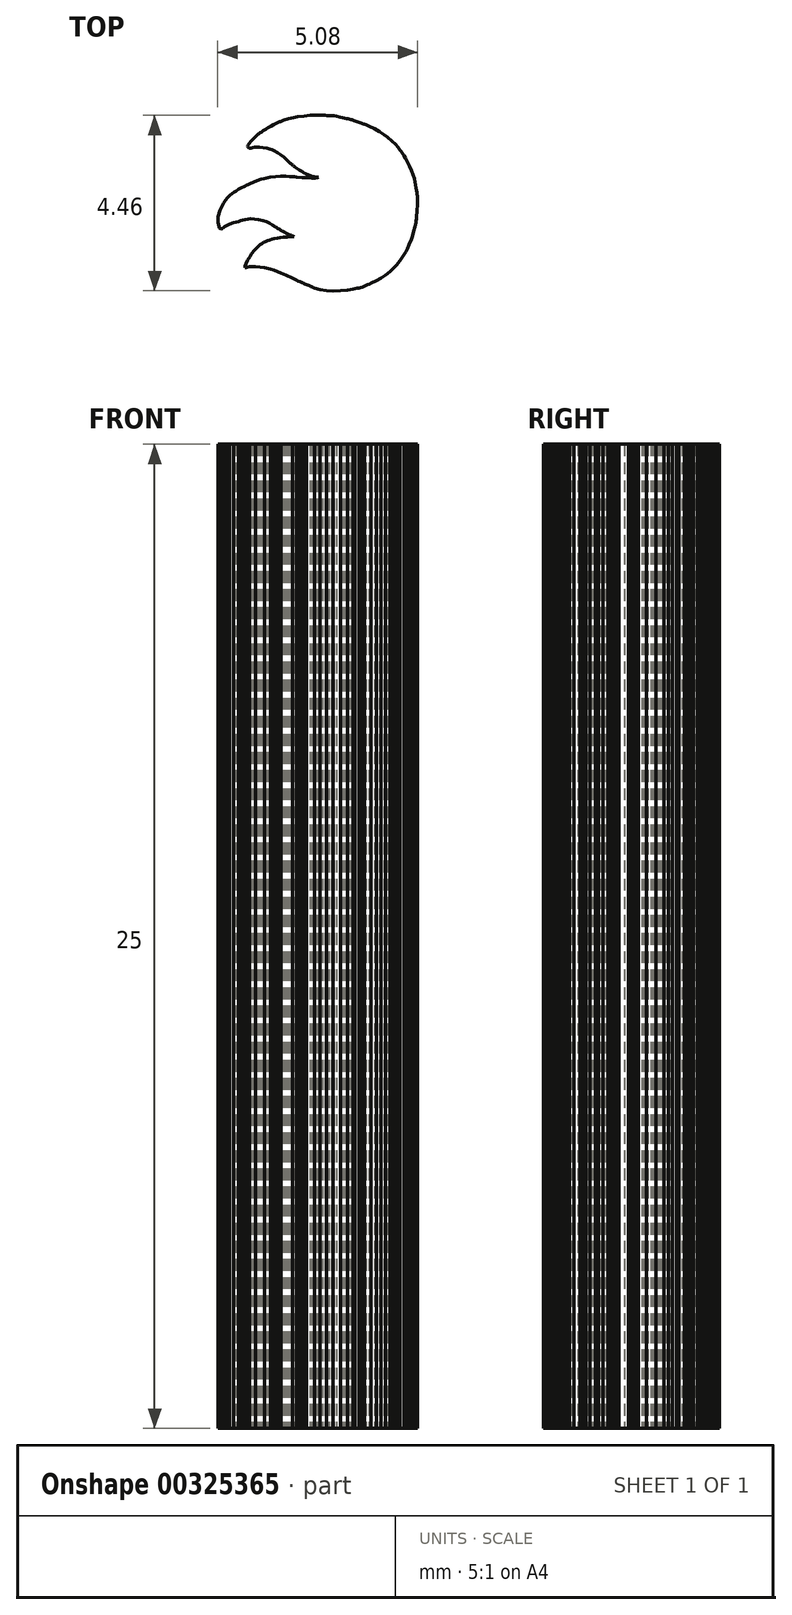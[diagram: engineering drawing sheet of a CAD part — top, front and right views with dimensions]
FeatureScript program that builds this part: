
annotation { "Feature Type Name" : "Feature", "Feature Type Description" : "" }
export const myFeature = defineFeature(function(context is Context, id is Id, definition is map)
    precondition{}
    {
        {
            var Q0;
            Q0=qCreatedBy(makeId("Top.planeOp"),FACE);
            var sketch = newSketch(context, id + "F0", { "sketchPlane" : qUnion([Q0])});
            skLineSegment(sketch, "E0.bottom", {"start": v(-35.48, 36.06) * mm, "end": v(-0.48, 36.06) * mm});
            skLineSegment(sketch, "E0.top", {"start": v(-35.48, 6.06) * mm, "end": v(-0.48, 6.06) * mm});
            skLineSegment(sketch, "E0.left", {"start": v(-35.48, 36.06) * mm, "end": v(-35.48, 6.06) * mm});
            skLineSegment(sketch, "E0.right", {"start": v(-0.48, 36.06) * mm, "end": v(-0.48, 6.06) * mm});
            skPoint(sketch, "E1", {"position": v(-0.48, 21.06) * mm});
            skArc(sketch, "E2", {"start": v(-0.48, 6.06) * mm, "mid": v(14.52, 21.06) * mm, "end": v(-0.48, 36.06) * mm});
            skLineSegment(sketch, "E3", {"start": v(0.23, -2.23) * mm, "end": v(0.06, -2.2) * mm});
            skLineSegment(sketch, "E4", {"start": v(0.06, -2.2) * mm, "end": v(-0.08, -2.16) * mm});
            skLineSegment(sketch, "E5", {"start": v(-0.08, -2.16) * mm, "end": v(-0.1, -2.16) * mm});
            skLineSegment(sketch, "E6", {"start": v(-0.1, -2.16) * mm, "end": v(-0.1, -2.15) * mm});
            skLineSegment(sketch, "E7", {"start": v(-0.1, -2.15) * mm, "end": v(-0.12, -2.14) * mm});
            skLineSegment(sketch, "E8", {"start": v(-0.12, -2.14) * mm, "end": v(-0.13, -2.14) * mm});
            skLineSegment(sketch, "E9", {"start": v(-0.13, -2.14) * mm, "end": v(-0.15, -2.13) * mm});
            skLineSegment(sketch, "E10", {"start": v(-0.15, -2.13) * mm, "end": v(-0.18, -2.12) * mm});
            skLineSegment(sketch, "E11", {"start": v(-0.18, -2.12) * mm, "end": v(-0.2, -2.1) * mm});
            skLineSegment(sketch, "E12", {"start": v(-0.2, -2.1) * mm, "end": v(-0.25, -2.09) * mm});
            skLineSegment(sketch, "E13", {"start": v(-0.25, -2.09) * mm, "end": v(-0.29, -2.07) * mm});
            skLineSegment(sketch, "E14", {"start": v(-0.29, -2.07) * mm, "end": v(-0.32, -2.06) * mm});
            skLineSegment(sketch, "E15", {"start": v(-0.32, -2.06) * mm, "end": v(-0.34, -2.04) * mm});
            skLineSegment(sketch, "E16", {"start": v(-0.34, -2.04) * mm, "end": v(-0.36, -2.04) * mm});
            skLineSegment(sketch, "E17", {"start": v(-0.36, -2.04) * mm, "end": v(-0.38, -2.03) * mm});
            skLineSegment(sketch, "E18", {"start": v(-0.38, -2.03) * mm, "end": v(-0.4, -2.02) * mm});
            skLineSegment(sketch, "E19", {"start": v(-0.4, -2.02) * mm, "end": v(-0.45, -2) * mm});
            skLineSegment(sketch, "E20", {"start": v(-0.45, -2) * mm, "end": v(-0.5, -1.98) * mm});
            skLineSegment(sketch, "E21", {"start": v(-0.5, -1.98) * mm, "end": v(-0.54, -1.96) * mm});
            skLineSegment(sketch, "E22", {"start": v(-0.54, -1.96) * mm, "end": v(-0.64, -1.91) * mm});
            skLineSegment(sketch, "E23", {"start": v(-0.64, -1.91) * mm, "end": v(-0.81, -1.83) * mm});
            skLineSegment(sketch, "E24", {"start": v(-0.81, -1.83) * mm, "end": v(-0.93, -1.78) * mm});
            skLineSegment(sketch, "E25", {"start": v(-0.93, -1.78) * mm, "end": v(-1.03, -1.74) * mm});
            skLineSegment(sketch, "E26", {"start": v(-1.03, -1.74) * mm, "end": v(-1.1, -1.7) * mm});
            skLineSegment(sketch, "E27", {"start": v(-1.1, -1.7) * mm, "end": v(-1.2, -1.68) * mm});
            skLineSegment(sketch, "E28", {"start": v(-1.2, -1.68) * mm, "end": v(-1.35, -1.65) * mm});
            skLineSegment(sketch, "E29", {"start": v(-1.35, -1.65) * mm, "end": v(-1.58, -1.62) * mm});
            skLineSegment(sketch, "E30", {"start": v(-1.58, -1.62) * mm, "end": v(-1.73, -1.61) * mm});
            skLineSegment(sketch, "E31", {"start": v(-1.73, -1.61) * mm, "end": v(-1.82, -1.64) * mm});
            skLineSegment(sketch, "E32", {"start": v(-1.82, -1.64) * mm, "end": v(-1.83, -1.65) * mm});
            skLineSegment(sketch, "E33", {"start": v(-1.83, -1.65) * mm, "end": v(-1.84, -1.64) * mm});
            skLineSegment(sketch, "E34", {"start": v(-1.84, -1.64) * mm, "end": v(-1.85, -1.62) * mm});
            skLineSegment(sketch, "E35", {"start": v(-1.85, -1.62) * mm, "end": v(-1.84, -1.6) * mm});
            skLineSegment(sketch, "E36", {"start": v(-1.84, -1.6) * mm, "end": v(-1.82, -1.54) * mm});
            skLineSegment(sketch, "E37", {"start": v(-1.82, -1.54) * mm, "end": v(-1.78, -1.45) * mm});
            skLineSegment(sketch, "E38", {"start": v(-1.78, -1.45) * mm, "end": v(-1.73, -1.36) * mm});
            skLineSegment(sketch, "E39", {"start": v(-1.73, -1.36) * mm, "end": v(-1.68, -1.28) * mm});
            skLineSegment(sketch, "E40", {"start": v(-1.68, -1.28) * mm, "end": v(-1.6, -1.2) * mm});
            skLineSegment(sketch, "E41", {"start": v(-1.6, -1.2) * mm, "end": v(-1.53, -1.12) * mm});
            skLineSegment(sketch, "E42", {"start": v(-1.53, -1.12) * mm, "end": v(-1.47, -1.06) * mm});
            skLineSegment(sketch, "E43", {"start": v(-1.47, -1.06) * mm, "end": v(-1.42, -1.03) * mm});
            skLineSegment(sketch, "E44", {"start": v(-1.42, -1.03) * mm, "end": v(-1.4, -1.02) * mm});
            skLineSegment(sketch, "E45", {"start": v(-1.4, -1.02) * mm, "end": v(-1.4, -1) * mm});
            skLineSegment(sketch, "E46", {"start": v(-1.4, -1) * mm, "end": v(-1.38, -1) * mm});
            skLineSegment(sketch, "E47", {"start": v(-1.38, -1) * mm, "end": v(-1.36, -1) * mm});
            skLineSegment(sketch, "E48", {"start": v(-1.36, -1) * mm, "end": v(-1.33, -0.98) * mm});
            skLineSegment(sketch, "E49", {"start": v(-1.33, -0.98) * mm, "end": v(-1.28, -0.96) * mm});
            skLineSegment(sketch, "E50", {"start": v(-1.28, -0.96) * mm, "end": v(-1.22, -0.94) * mm});
            skLineSegment(sketch, "E51", {"start": v(-1.22, -0.94) * mm, "end": v(-1.16, -0.92) * mm});
            skLineSegment(sketch, "E52", {"start": v(-1.16, -0.92) * mm, "end": v(-1.1, -0.9) * mm});
            skLineSegment(sketch, "E53", {"start": v(-1.1, -0.9) * mm, "end": v(-1.02, -0.9) * mm});
            skLineSegment(sketch, "E54", {"start": v(-1.02, -0.9) * mm, "end": v(-0.95, -0.88) * mm});
            skLineSegment(sketch, "E55", {"start": v(-0.95, -0.88) * mm, "end": v(-0.88, -0.87) * mm});
            skLineSegment(sketch, "E56", {"start": v(-0.88, -0.87) * mm, "end": v(-0.78, -0.86) * mm});
            skLineSegment(sketch, "E57", {"start": v(-0.78, -0.86) * mm, "end": v(-0.74, -0.86) * mm});
            skLineSegment(sketch, "E58", {"start": v(-0.74, -0.86) * mm, "end": v(-0.67, -0.86) * mm});
            skLineSegment(sketch, "E59", {"start": v(-0.67, -0.86) * mm, "end": v(-0.63, -0.86) * mm});
            skLineSegment(sketch, "E60", {"start": v(-0.63, -0.86) * mm, "end": v(-0.6, -0.85) * mm});
            skLineSegment(sketch, "E61", {"start": v(-0.6, -0.85) * mm, "end": v(-0.6, -0.85) * mm});
            skLineSegment(sketch, "E62", {"start": v(-0.6, -0.85) * mm, "end": v(-0.61, -0.85) * mm});
            skLineSegment(sketch, "E63", {"start": v(-0.61, -0.85) * mm, "end": v(-0.63, -0.84) * mm});
            skLineSegment(sketch, "E64", {"start": v(-0.63, -0.84) * mm, "end": v(-0.65, -0.83) * mm});
            skLineSegment(sketch, "E65", {"start": v(-0.65, -0.83) * mm, "end": v(-0.67, -0.82) * mm});
            skLineSegment(sketch, "E66", {"start": v(-0.67, -0.82) * mm, "end": v(-0.68, -0.82) * mm});
            skLineSegment(sketch, "E67", {"start": v(-0.68, -0.82) * mm, "end": v(-0.7, -0.81) * mm});
            skLineSegment(sketch, "E68", {"start": v(-0.7, -0.81) * mm, "end": v(-0.72, -0.8) * mm});
            skLineSegment(sketch, "E69", {"start": v(-0.72, -0.8) * mm, "end": v(-0.76, -0.79) * mm});
            skLineSegment(sketch, "E70", {"start": v(-0.76, -0.79) * mm, "end": v(-0.8, -0.77) * mm});
            skLineSegment(sketch, "E71", {"start": v(-0.8, -0.77) * mm, "end": v(-0.84, -0.75) * mm});
            skLineSegment(sketch, "E72", {"start": v(-0.84, -0.75) * mm, "end": v(-0.87, -0.73) * mm});
            skLineSegment(sketch, "E73", {"start": v(-0.87, -0.73) * mm, "end": v(-0.9, -0.71) * mm});
            skLineSegment(sketch, "E74", {"start": v(-0.9, -0.71) * mm, "end": v(-0.9, -0.7) * mm});
            skLineSegment(sketch, "E75", {"start": v(-0.9, -0.7) * mm, "end": v(-0.92, -0.7) * mm});
            skLineSegment(sketch, "E76", {"start": v(-0.92, -0.7) * mm, "end": v(-0.94, -0.69) * mm});
            skLineSegment(sketch, "E77", {"start": v(-0.94, -0.69) * mm, "end": v(-0.98, -0.67) * mm});
            skLineSegment(sketch, "E78", {"start": v(-0.98, -0.67) * mm, "end": v(-1, -0.65) * mm});
            skLineSegment(sketch, "E79", {"start": v(-1, -0.65) * mm, "end": v(-1.03, -0.64) * mm});
            skLineSegment(sketch, "E80", {"start": v(-1.03, -0.64) * mm, "end": v(-1.04, -0.63) * mm});
            skLineSegment(sketch, "E81", {"start": v(-1.04, -0.63) * mm, "end": v(-1.06, -0.62) * mm});
            skLineSegment(sketch, "E82", {"start": v(-1.06, -0.62) * mm, "end": v(-1.07, -0.6) * mm});
            skLineSegment(sketch, "E83", {"start": v(-1.07, -0.6) * mm, "end": v(-1.08, -0.6) * mm});
            skLineSegment(sketch, "E84", {"start": v(-1.08, -0.6) * mm, "end": v(-1.1, -0.6) * mm});
            skLineSegment(sketch, "E85", {"start": v(-1.1, -0.6) * mm, "end": v(-1.1, -0.59) * mm});
            skLineSegment(sketch, "E86", {"start": v(-1.1, -0.59) * mm, "end": v(-1.13, -0.57) * mm});
            skLineSegment(sketch, "E87", {"start": v(-1.13, -0.57) * mm, "end": v(-1.15, -0.56) * mm});
            skLineSegment(sketch, "E88", {"start": v(-1.15, -0.56) * mm, "end": v(-1.22, -0.51) * mm});
            skLineSegment(sketch, "E89", {"start": v(-1.22, -0.51) * mm, "end": v(-1.3, -0.48) * mm});
            skLineSegment(sketch, "E90", {"start": v(-1.3, -0.48) * mm, "end": v(-1.4, -0.45) * mm});
            skLineSegment(sketch, "E91", {"start": v(-1.4, -0.45) * mm, "end": v(-1.5, -0.42) * mm});
            skLineSegment(sketch, "E92", {"start": v(-1.5, -0.42) * mm, "end": v(-1.7, -0.4) * mm});
            skLineSegment(sketch, "E93", {"start": v(-1.7, -0.4) * mm, "end": v(-1.91, -0.44) * mm});
            skLineSegment(sketch, "E94", {"start": v(-1.91, -0.44) * mm, "end": v(-1.96, -0.45) * mm});
            skLineSegment(sketch, "E95", {"start": v(-1.96, -0.45) * mm, "end": v(-2.02, -0.47) * mm});
            skLineSegment(sketch, "E96", {"start": v(-2.02, -0.47) * mm, "end": v(-2.14, -0.5) * mm});
            skLineSegment(sketch, "E97", {"start": v(-2.14, -0.5) * mm, "end": v(-2.24, -0.54) * mm});
            skLineSegment(sketch, "E98", {"start": v(-2.24, -0.54) * mm, "end": v(-2.31, -0.57) * mm});
            skLineSegment(sketch, "E99", {"start": v(-2.31, -0.57) * mm, "end": v(-2.36, -0.6) * mm});
            skLineSegment(sketch, "E100", {"start": v(-2.36, -0.6) * mm, "end": v(-2.4, -0.63) * mm});
            skLineSegment(sketch, "E101", {"start": v(-2.4, -0.63) * mm, "end": v(-2.4, -0.64) * mm});
            skLineSegment(sketch, "E102", {"start": v(-2.4, -0.64) * mm, "end": v(-2.42, -0.64) * mm});
            skLineSegment(sketch, "E103", {"start": v(-2.42, -0.64) * mm, "end": v(-2.42, -0.65) * mm});
            skLineSegment(sketch, "E104", {"start": v(-2.42, -0.65) * mm, "end": v(-2.43, -0.65) * mm});
            skLineSegment(sketch, "E105", {"start": v(-2.43, -0.65) * mm, "end": v(-2.45, -0.66) * mm});
            skLineSegment(sketch, "E106", {"start": v(-2.45, -0.66) * mm, "end": v(-2.47, -0.66) * mm});
            skLineSegment(sketch, "E107", {"start": v(-2.47, -0.66) * mm, "end": v(-2.49, -0.65) * mm});
            skLineSegment(sketch, "E108", {"start": v(-2.49, -0.65) * mm, "end": v(-2.5, -0.63) * mm});
            skLineSegment(sketch, "E109", {"start": v(-2.5, -0.63) * mm, "end": v(-2.51, -0.6) * mm});
            skLineSegment(sketch, "E110", {"start": v(-2.51, -0.6) * mm, "end": v(-2.54, -0.48) * mm});
            skLineSegment(sketch, "E111", {"start": v(-2.54, -0.48) * mm, "end": v(-2.53, -0.34) * mm});
            skLineSegment(sketch, "E112", {"start": v(-2.53, -0.34) * mm, "end": v(-2.48, -0.18) * mm});
            skLineSegment(sketch, "E113", {"start": v(-2.48, -0.18) * mm, "end": v(-2.4, 0) * mm});
            skLineSegment(sketch, "E114", {"start": v(-2.4, 0) * mm, "end": v(-2.34, 0.07) * mm});
            skLineSegment(sketch, "E115", {"start": v(-2.34, 0.07) * mm, "end": v(-2.29, 0.14) * mm});
            skLineSegment(sketch, "E116", {"start": v(-2.29, 0.14) * mm, "end": v(-2.22, 0.2) * mm});
            skLineSegment(sketch, "E117", {"start": v(-2.22, 0.2) * mm, "end": v(-2.13, 0.27) * mm});
            skLineSegment(sketch, "E118", {"start": v(-2.13, 0.27) * mm, "end": v(-2.08, 0.3) * mm});
            skLineSegment(sketch, "E119", {"start": v(-2.08, 0.3) * mm, "end": v(-2.01, 0.35) * mm});
            skLineSegment(sketch, "E120", {"start": v(-2.01, 0.35) * mm, "end": v(-1.94, 0.39) * mm});
            skLineSegment(sketch, "E121", {"start": v(-1.94, 0.39) * mm, "end": v(-1.87, 0.42) * mm});
            skLineSegment(sketch, "E122", {"start": v(-1.87, 0.42) * mm, "end": v(-1.85, 0.43) * mm});
            skLineSegment(sketch, "E123", {"start": v(-1.85, 0.43) * mm, "end": v(-1.8, 0.45) * mm});
            skLineSegment(sketch, "E124", {"start": v(-1.8, 0.45) * mm, "end": v(-1.77, 0.47) * mm});
            skLineSegment(sketch, "E125", {"start": v(-1.77, 0.47) * mm, "end": v(-1.72, 0.5) * mm});
            skLineSegment(sketch, "E126", {"start": v(-1.72, 0.5) * mm, "end": v(-1.64, 0.53) * mm});
            skLineSegment(sketch, "E127", {"start": v(-1.64, 0.53) * mm, "end": v(-1.54, 0.57) * mm});
            skLineSegment(sketch, "E128", {"start": v(-1.54, 0.57) * mm, "end": v(-1.44, 0.6) * mm});
            skLineSegment(sketch, "E129", {"start": v(-1.44, 0.6) * mm, "end": v(-1.37, 0.62) * mm});
            skLineSegment(sketch, "E130", {"start": v(-1.37, 0.62) * mm, "end": v(-1.2, 0.65) * mm});
            skLineSegment(sketch, "E131", {"start": v(-1.2, 0.65) * mm, "end": v(-1.07, 0.67) * mm});
            skLineSegment(sketch, "E132", {"start": v(-1.07, 0.67) * mm, "end": v(-0.95, 0.68) * mm});
            skLineSegment(sketch, "E133", {"start": v(-0.95, 0.68) * mm, "end": v(-0.8, 0.68) * mm});
            skLineSegment(sketch, "E134", {"start": v(-0.8, 0.68) * mm, "end": v(-0.72, 0.68) * mm});
            skLineSegment(sketch, "E135", {"start": v(-0.72, 0.68) * mm, "end": v(-0.65, 0.67) * mm});
            skLineSegment(sketch, "E136", {"start": v(-0.65, 0.67) * mm, "end": v(-0.58, 0.67) * mm});
            skLineSegment(sketch, "E137", {"start": v(-0.58, 0.67) * mm, "end": v(-0.54, 0.66) * mm});
            skLineSegment(sketch, "E138", {"start": v(-0.54, 0.66) * mm, "end": v(-0.4, 0.65) * mm});
            skLineSegment(sketch, "E139", {"start": v(-0.4, 0.65) * mm, "end": v(-0.27, 0.64) * mm});
            skLineSegment(sketch, "E140", {"start": v(-0.27, 0.64) * mm, "end": v(-0.16, 0.64) * mm});
            skLineSegment(sketch, "E141", {"start": v(-0.16, 0.64) * mm, "end": v(-0.07, 0.64) * mm});
            skLineSegment(sketch, "E142", {"start": v(-0.07, 0.64) * mm, "end": v(-0.01, 0.64) * mm});
            skLineSegment(sketch, "E143", {"start": v(-0.01, 0.64) * mm, "end": v(0.02, 0.65) * mm});
            skLineSegment(sketch, "E144", {"start": v(0.02, 0.65) * mm, "end": v(0, 0.66) * mm});
            skLineSegment(sketch, "E145", {"start": v(0, 0.66) * mm, "end": v(-0.04, 0.66) * mm});
            skLineSegment(sketch, "E146", {"start": v(-0.04, 0.66) * mm, "end": v(-0.09, 0.67) * mm});
            skLineSegment(sketch, "E147", {"start": v(-0.09, 0.67) * mm, "end": v(-0.14, 0.67) * mm});
            skLineSegment(sketch, "E148", {"start": v(-0.14, 0.67) * mm, "end": v(-0.19, 0.7) * mm});
            skLineSegment(sketch, "E149", {"start": v(-0.19, 0.7) * mm, "end": v(-0.25, 0.72) * mm});
            skLineSegment(sketch, "E150", {"start": v(-0.25, 0.72) * mm, "end": v(-0.29, 0.74) * mm});
            skLineSegment(sketch, "E151", {"start": v(-0.29, 0.74) * mm, "end": v(-0.3, 0.74) * mm});
            skLineSegment(sketch, "E152", {"start": v(-0.3, 0.74) * mm, "end": v(-0.32, 0.75) * mm});
            skLineSegment(sketch, "E153", {"start": v(-0.32, 0.75) * mm, "end": v(-0.36, 0.77) * mm});
            skLineSegment(sketch, "E154", {"start": v(-0.36, 0.77) * mm, "end": v(-0.39, 0.8) * mm});
            skLineSegment(sketch, "E155", {"start": v(-0.39, 0.8) * mm, "end": v(-0.4, 0.8) * mm});
            skLineSegment(sketch, "E156", {"start": v(-0.4, 0.8) * mm, "end": v(-0.42, 0.8) * mm});
            skLineSegment(sketch, "E157", {"start": v(-0.42, 0.8) * mm, "end": v(-0.44, 0.82) * mm});
            skLineSegment(sketch, "E158", {"start": v(-0.44, 0.82) * mm, "end": v(-0.47, 0.84) * mm});
            skLineSegment(sketch, "E159", {"start": v(-0.47, 0.84) * mm, "end": v(-0.5, 0.86) * mm});
            skLineSegment(sketch, "E160", {"start": v(-0.5, 0.86) * mm, "end": v(-0.54, 0.89) * mm});
            skLineSegment(sketch, "E161", {"start": v(-0.54, 0.89) * mm, "end": v(-0.57, 0.91) * mm});
            skLineSegment(sketch, "E162", {"start": v(-0.57, 0.91) * mm, "end": v(-0.6, 0.93) * mm});
            skLineSegment(sketch, "E163", {"start": v(-0.6, 0.93) * mm, "end": v(-0.6, 0.94) * mm});
            skLineSegment(sketch, "E164", {"start": v(-0.6, 0.94) * mm, "end": v(-0.63, 0.96) * mm});
            skLineSegment(sketch, "E165", {"start": v(-0.63, 0.96) * mm, "end": v(-0.66, 0.98) * mm});
            skLineSegment(sketch, "E166", {"start": v(-0.66, 0.98) * mm, "end": v(-0.68, 1) * mm});
            skLineSegment(sketch, "E167", {"start": v(-0.68, 1) * mm, "end": v(-0.7, 1.01) * mm});
            skLineSegment(sketch, "E168", {"start": v(-0.7, 1.01) * mm, "end": v(-0.73, 1.04) * mm});
            skLineSegment(sketch, "E169", {"start": v(-0.73, 1.04) * mm, "end": v(-0.75, 1.06) * mm});
            skLineSegment(sketch, "E170", {"start": v(-0.75, 1.06) * mm, "end": v(-0.86, 1.16) * mm});
            skLineSegment(sketch, "E171", {"start": v(-0.86, 1.16) * mm, "end": v(-0.94, 1.23) * mm});
            skLineSegment(sketch, "E172", {"start": v(-0.94, 1.23) * mm, "end": v(-1.02, 1.28) * mm});
            skLineSegment(sketch, "E173", {"start": v(-1.02, 1.28) * mm, "end": v(-1.12, 1.33) * mm});
            skLineSegment(sketch, "E174", {"start": v(-1.12, 1.33) * mm, "end": v(-1.16, 1.35) * mm});
            skLineSegment(sketch, "E175", {"start": v(-1.16, 1.35) * mm, "end": v(-1.2, 1.37) * mm});
            skLineSegment(sketch, "E176", {"start": v(-1.2, 1.37) * mm, "end": v(-1.29, 1.39) * mm});
            skLineSegment(sketch, "E177", {"start": v(-1.29, 1.39) * mm, "end": v(-1.39, 1.4) * mm});
            skLineSegment(sketch, "E178", {"start": v(-1.39, 1.4) * mm, "end": v(-1.48, 1.42) * mm});
            skLineSegment(sketch, "E179", {"start": v(-1.48, 1.42) * mm, "end": v(-1.55, 1.42) * mm});
            skLineSegment(sketch, "E180", {"start": v(-1.55, 1.42) * mm, "end": v(-1.6, 1.42) * mm});
            skLineSegment(sketch, "E181", {"start": v(-1.6, 1.42) * mm, "end": v(-1.65, 1.41) * mm});
            skLineSegment(sketch, "E182", {"start": v(-1.65, 1.41) * mm, "end": v(-1.7, 1.4) * mm});
            skLineSegment(sketch, "E183", {"start": v(-1.7, 1.4) * mm, "end": v(-1.73, 1.39) * mm});
            skLineSegment(sketch, "E184", {"start": v(-1.73, 1.39) * mm, "end": v(-1.74, 1.4) * mm});
            skLineSegment(sketch, "E185", {"start": v(-1.74, 1.4) * mm, "end": v(-1.76, 1.4) * mm});
            skLineSegment(sketch, "E186", {"start": v(-1.76, 1.4) * mm, "end": v(-1.77, 1.42) * mm});
            skLineSegment(sketch, "E187", {"start": v(-1.77, 1.42) * mm, "end": v(-1.78, 1.44) * mm});
            skLineSegment(sketch, "E188", {"start": v(-1.78, 1.44) * mm, "end": v(-1.77, 1.47) * mm});
            skLineSegment(sketch, "E189", {"start": v(-1.77, 1.47) * mm, "end": v(-1.74, 1.51) * mm});
            skLineSegment(sketch, "E190", {"start": v(-1.74, 1.51) * mm, "end": v(-1.7, 1.57) * mm});
            skLineSegment(sketch, "E191", {"start": v(-1.7, 1.57) * mm, "end": v(-1.64, 1.62) * mm});
            skLineSegment(sketch, "E192", {"start": v(-1.64, 1.62) * mm, "end": v(-1.6, 1.68) * mm});
            skLineSegment(sketch, "E193", {"start": v(-1.6, 1.68) * mm, "end": v(-1.55, 1.72) * mm});
            skLineSegment(sketch, "E194", {"start": v(-1.55, 1.72) * mm, "end": v(-1.51, 1.75) * mm});
            skLineSegment(sketch, "E195", {"start": v(-1.51, 1.75) * mm, "end": v(-1.5, 1.76) * mm});
            skLineSegment(sketch, "E196", {"start": v(-1.5, 1.76) * mm, "end": v(-1.49, 1.77) * mm});
            skLineSegment(sketch, "E197", {"start": v(-1.49, 1.77) * mm, "end": v(-1.46, 1.78) * mm});
            skLineSegment(sketch, "E198", {"start": v(-1.46, 1.78) * mm, "end": v(-1.43, 1.8) * mm});
            skLineSegment(sketch, "E199", {"start": v(-1.43, 1.8) * mm, "end": v(-1.39, 1.83) * mm});
            skLineSegment(sketch, "E200", {"start": v(-1.39, 1.83) * mm, "end": v(-1.34, 1.86) * mm});
            skLineSegment(sketch, "E201", {"start": v(-1.34, 1.86) * mm, "end": v(-1.31, 1.88) * mm});
            skLineSegment(sketch, "E202", {"start": v(-1.31, 1.88) * mm, "end": v(-1.29, 1.9) * mm});
            skLineSegment(sketch, "E203", {"start": v(-1.29, 1.9) * mm, "end": v(-1.28, 1.9) * mm});
            skLineSegment(sketch, "E204", {"start": v(-1.28, 1.9) * mm, "end": v(-1.26, 1.9) * mm});
            skLineSegment(sketch, "E205", {"start": v(-1.26, 1.9) * mm, "end": v(-1.24, 1.92) * mm});
            skLineSegment(sketch, "E206", {"start": v(-1.24, 1.92) * mm, "end": v(-1.2, 1.95) * mm});
            skLineSegment(sketch, "E207", {"start": v(-1.2, 1.95) * mm, "end": v(-1.12, 2) * mm});
            skLineSegment(sketch, "E208", {"start": v(-1.12, 2) * mm, "end": v(-1.05, 2.03) * mm});
            skLineSegment(sketch, "E209", {"start": v(-1.05, 2.03) * mm, "end": v(-1, 2.05) * mm});
            skLineSegment(sketch, "E210", {"start": v(-1, 2.05) * mm, "end": v(-0.97, 2.06) * mm});
            skLineSegment(sketch, "E211", {"start": v(-0.97, 2.06) * mm, "end": v(-0.95, 2.07) * mm});
            skLineSegment(sketch, "E212", {"start": v(-0.95, 2.07) * mm, "end": v(-0.86, 2.1) * mm});
            skLineSegment(sketch, "E213", {"start": v(-0.86, 2.1) * mm, "end": v(-0.75, 2.14) * mm});
            skLineSegment(sketch, "E214", {"start": v(-0.75, 2.14) * mm, "end": v(-0.62, 2.17) * mm});
            skLineSegment(sketch, "E215", {"start": v(-0.62, 2.17) * mm, "end": v(-0.52, 2.2) * mm});
            skLineSegment(sketch, "E216", {"start": v(-0.52, 2.2) * mm, "end": v(-0.35, 2.21) * mm});
            skLineSegment(sketch, "E217", {"start": v(-0.35, 2.21) * mm, "end": v(-0.2, 2.23) * mm});
            skLineSegment(sketch, "E218", {"start": v(-0.2, 2.23) * mm, "end": v(-0.04, 2.23) * mm});
            skLineSegment(sketch, "E219", {"start": v(-0.04, 2.23) * mm, "end": v(0.08, 2.23) * mm});
            skLineSegment(sketch, "E220", {"start": v(0.08, 2.23) * mm, "end": v(0.12, 2.23) * mm});
            skLineSegment(sketch, "E221", {"start": v(0.12, 2.23) * mm, "end": v(0.18, 2.23) * mm});
            skLineSegment(sketch, "E222", {"start": v(0.18, 2.23) * mm, "end": v(0.24, 2.22) * mm});
            skLineSegment(sketch, "E223", {"start": v(0.24, 2.22) * mm, "end": v(0.29, 2.22) * mm});
            skLineSegment(sketch, "E224", {"start": v(0.29, 2.22) * mm, "end": v(0.35, 2.22) * mm});
            skLineSegment(sketch, "E225", {"start": v(0.35, 2.22) * mm, "end": v(0.41, 2.22) * mm});
            skLineSegment(sketch, "E226", {"start": v(0.41, 2.22) * mm, "end": v(0.48, 2.2) * mm});
            skLineSegment(sketch, "E227", {"start": v(0.48, 2.2) * mm, "end": v(0.56, 2.18) * mm});
            skLineSegment(sketch, "E228", {"start": v(0.56, 2.18) * mm, "end": v(0.63, 2.17) * mm});
            skLineSegment(sketch, "E229", {"start": v(0.63, 2.17) * mm, "end": v(0.68, 2.15) * mm});
            skLineSegment(sketch, "E230", {"start": v(0.68, 2.15) * mm, "end": v(0.73, 2.15) * mm});
            skLineSegment(sketch, "E231", {"start": v(0.73, 2.15) * mm, "end": v(0.75, 2.14) * mm});
            skLineSegment(sketch, "E232", {"start": v(0.75, 2.14) * mm, "end": v(0.77, 2.14) * mm});
            skLineSegment(sketch, "E233", {"start": v(0.77, 2.14) * mm, "end": v(0.8, 2.13) * mm});
            skLineSegment(sketch, "E234", {"start": v(0.8, 2.13) * mm, "end": v(0.84, 2.12) * mm});
            skLineSegment(sketch, "E235", {"start": v(0.84, 2.12) * mm, "end": v(0.87, 2.11) * mm});
            skLineSegment(sketch, "E236", {"start": v(0.87, 2.11) * mm, "end": v(0.89, 2.1) * mm});
            skLineSegment(sketch, "E237", {"start": v(0.89, 2.1) * mm, "end": v(0.92, 2.1) * mm});
            skLineSegment(sketch, "E238", {"start": v(0.92, 2.1) * mm, "end": v(0.95, 2.09) * mm});
            skLineSegment(sketch, "E239", {"start": v(0.95, 2.09) * mm, "end": v(1, 2.07) * mm});
            skLineSegment(sketch, "E240", {"start": v(1, 2.07) * mm, "end": v(1.04, 2.06) * mm});
            skLineSegment(sketch, "E241", {"start": v(1.04, 2.06) * mm, "end": v(1.08, 2.04) * mm});
            skLineSegment(sketch, "E242", {"start": v(1.08, 2.04) * mm, "end": v(1.11, 2.03) * mm});
            skLineSegment(sketch, "E243", {"start": v(1.11, 2.03) * mm, "end": v(1.14, 2.02) * mm});
            skLineSegment(sketch, "E244", {"start": v(1.14, 2.02) * mm, "end": v(1.17, 2) * mm});
            skLineSegment(sketch, "E245", {"start": v(1.17, 2) * mm, "end": v(1.19, 2) * mm});
            skLineSegment(sketch, "E246", {"start": v(1.19, 2) * mm, "end": v(1.2, 2) * mm});
            skLineSegment(sketch, "E247", {"start": v(1.2, 2) * mm, "end": v(1.22, 2) * mm});
            skLineSegment(sketch, "E248", {"start": v(1.22, 2) * mm, "end": v(1.23, 1.99) * mm});
            skLineSegment(sketch, "E249", {"start": v(1.23, 1.99) * mm, "end": v(1.25, 1.98) * mm});
            skLineSegment(sketch, "E250", {"start": v(1.25, 1.98) * mm, "end": v(1.28, 1.97) * mm});
            skLineSegment(sketch, "E251", {"start": v(1.28, 1.97) * mm, "end": v(1.3, 1.95) * mm});
            skLineSegment(sketch, "E252", {"start": v(1.3, 1.95) * mm, "end": v(1.44, 1.89) * mm});
            skLineSegment(sketch, "E253", {"start": v(1.44, 1.89) * mm, "end": v(1.57, 1.82) * mm});
            skLineSegment(sketch, "E254", {"start": v(1.57, 1.82) * mm, "end": v(1.68, 1.74) * mm});
            skLineSegment(sketch, "E255", {"start": v(1.68, 1.74) * mm, "end": v(1.77, 1.67) * mm});
            skLineSegment(sketch, "E256", {"start": v(1.77, 1.67) * mm, "end": v(1.88, 1.58) * mm});
            skLineSegment(sketch, "E257", {"start": v(1.88, 1.58) * mm, "end": v(1.97, 1.5) * mm});
            skLineSegment(sketch, "E258", {"start": v(1.97, 1.5) * mm, "end": v(2.04, 1.41) * mm});
            skLineSegment(sketch, "E259", {"start": v(2.04, 1.41) * mm, "end": v(2.1, 1.34) * mm});
            skLineSegment(sketch, "E260", {"start": v(2.1, 1.34) * mm, "end": v(2.12, 1.31) * mm});
            skLineSegment(sketch, "E261", {"start": v(2.12, 1.31) * mm, "end": v(2.14, 1.27) * mm});
            skLineSegment(sketch, "E262", {"start": v(2.14, 1.27) * mm, "end": v(2.17, 1.24) * mm});
            skLineSegment(sketch, "E263", {"start": v(2.17, 1.24) * mm, "end": v(2.19, 1.2) * mm});
            skLineSegment(sketch, "E264", {"start": v(2.19, 1.2) * mm, "end": v(2.23, 1.14) * mm});
            skLineSegment(sketch, "E265", {"start": v(2.23, 1.14) * mm, "end": v(2.28, 1.04) * mm});
            skLineSegment(sketch, "E266", {"start": v(2.28, 1.04) * mm, "end": v(2.34, 0.93) * mm});
            skLineSegment(sketch, "E267", {"start": v(2.34, 0.93) * mm, "end": v(2.39, 0.82) * mm});
            skLineSegment(sketch, "E268", {"start": v(2.39, 0.82) * mm, "end": v(2.45, 0.62) * mm});
            skLineSegment(sketch, "E269", {"start": v(2.45, 0.62) * mm, "end": v(2.5, 0.38) * mm});
            skLineSegment(sketch, "E270", {"start": v(2.5, 0.38) * mm, "end": v(2.5, 0.32) * mm});
            skLineSegment(sketch, "E271", {"start": v(2.5, 0.32) * mm, "end": v(2.52, 0.27) * mm});
            skLineSegment(sketch, "E272", {"start": v(2.52, 0.27) * mm, "end": v(2.52, 0.22) * mm});
            skLineSegment(sketch, "E273", {"start": v(2.52, 0.22) * mm, "end": v(2.53, 0.18) * mm});
            skLineSegment(sketch, "E274", {"start": v(2.53, 0.18) * mm, "end": v(2.54, 0.11) * mm});
            skLineSegment(sketch, "E275", {"start": v(2.54, 0.11) * mm, "end": v(2.54, 0.04) * mm});
            skLineSegment(sketch, "E276", {"start": v(2.54, 0.04) * mm, "end": v(2.54, 0) * mm});
            skLineSegment(sketch, "E277", {"start": v(2.54, 0) * mm, "end": v(2.53, -0.07) * mm});
            skLineSegment(sketch, "E278", {"start": v(2.53, -0.07) * mm, "end": v(2.53, -0.15) * mm});
            skLineSegment(sketch, "E279", {"start": v(2.53, -0.15) * mm, "end": v(2.52, -0.24) * mm});
            skLineSegment(sketch, "E280", {"start": v(2.52, -0.24) * mm, "end": v(2.51, -0.32) * mm});
            skLineSegment(sketch, "E281", {"start": v(2.51, -0.32) * mm, "end": v(2.5, -0.4) * mm});
            skLineSegment(sketch, "E282", {"start": v(2.5, -0.4) * mm, "end": v(2.5, -0.46) * mm});
            skLineSegment(sketch, "E283", {"start": v(2.5, -0.46) * mm, "end": v(2.5, -0.5) * mm});
            skLineSegment(sketch, "E284", {"start": v(2.5, -0.5) * mm, "end": v(2.47, -0.6) * mm});
            skLineSegment(sketch, "E285", {"start": v(2.47, -0.6) * mm, "end": v(2.44, -0.72) * mm});
            skLineSegment(sketch, "E286", {"start": v(2.44, -0.72) * mm, "end": v(2.4, -0.84) * mm});
            skLineSegment(sketch, "E287", {"start": v(2.4, -0.84) * mm, "end": v(2.38, -0.91) * mm});
            skLineSegment(sketch, "E288", {"start": v(2.38, -0.91) * mm, "end": v(2.32, -1.06) * mm});
            skLineSegment(sketch, "E289", {"start": v(2.32, -1.06) * mm, "end": v(2.28, -1.16) * mm});
            skLineSegment(sketch, "E290", {"start": v(2.28, -1.16) * mm, "end": v(2.24, -1.23) * mm});
            skLineSegment(sketch, "E291", {"start": v(2.24, -1.23) * mm, "end": v(2.19, -1.3) * mm});
            skLineSegment(sketch, "E292", {"start": v(2.19, -1.3) * mm, "end": v(2.08, -1.46) * mm});
            skLineSegment(sketch, "E293", {"start": v(2.08, -1.46) * mm, "end": v(2, -1.57) * mm});
            skLineSegment(sketch, "E294", {"start": v(2, -1.57) * mm, "end": v(1.92, -1.66) * mm});
            skLineSegment(sketch, "E295", {"start": v(1.92, -1.66) * mm, "end": v(1.84, -1.74) * mm});
            skLineSegment(sketch, "E296", {"start": v(1.84, -1.74) * mm, "end": v(1.72, -1.83) * mm});
            skLineSegment(sketch, "E297", {"start": v(1.72, -1.83) * mm, "end": v(1.61, -1.9) * mm});
            skLineSegment(sketch, "E298", {"start": v(1.61, -1.9) * mm, "end": v(1.5, -1.97) * mm});
            skLineSegment(sketch, "E299", {"start": v(1.5, -1.97) * mm, "end": v(1.35, -2.04) * mm});
            skLineSegment(sketch, "E300", {"start": v(1.35, -2.04) * mm, "end": v(1.3, -2.06) * mm});
            skLineSegment(sketch, "E301", {"start": v(1.3, -2.06) * mm, "end": v(1.26, -2.08) * mm});
            skLineSegment(sketch, "E302", {"start": v(1.26, -2.08) * mm, "end": v(1.22, -2.1) * mm});
            skLineSegment(sketch, "E303", {"start": v(1.22, -2.1) * mm, "end": v(1.18, -2.11) * mm});
            skLineSegment(sketch, "E304", {"start": v(1.18, -2.11) * mm, "end": v(1.13, -2.13) * mm});
            skLineSegment(sketch, "E305", {"start": v(1.13, -2.13) * mm, "end": v(1.1, -2.15) * mm});
            skLineSegment(sketch, "E306", {"start": v(1.1, -2.15) * mm, "end": v(1.05, -2.16) * mm});
            skLineSegment(sketch, "E307", {"start": v(1.05, -2.16) * mm, "end": v(1, -2.17) * mm});
            skLineSegment(sketch, "E308", {"start": v(1, -2.17) * mm, "end": v(0.95, -2.18) * mm});
            skLineSegment(sketch, "E309", {"start": v(0.95, -2.18) * mm, "end": v(0.9, -2.19) * mm});
            skLineSegment(sketch, "E310", {"start": v(0.9, -2.19) * mm, "end": v(0.76, -2.21) * mm});
            skLineSegment(sketch, "E311", {"start": v(0.76, -2.21) * mm, "end": v(0.58, -2.23) * mm});
            skLineSegment(sketch, "E312", {"start": v(0.58, -2.23) * mm, "end": v(0.39, -2.23) * mm});
            skLineSegment(sketch, "E313", {"start": v(0.39, -2.23) * mm, "end": v(0.23, -2.23) * mm});
            skLineSegment(sketch, "E314", {"start": v(-106.25, -53.48) * mm, "end": v(-133.58, -5.75) * mm});
            skPoint(sketch, "E315", {"position": v(-113.58, -40.68) * mm});
            skLineSegment(sketch, "E316.bottom", {"start": v(-113.58, -40.68) * mm, "end": v(-105.08, -40.68) * mm});
            skLineSegment(sketch, "E316.top", {"start": v(-113.58, -47.08) * mm, "end": v(-105.08, -47.08) * mm});
            skLineSegment(sketch, "E316.left", {"start": v(-113.58, -40.68) * mm, "end": v(-113.58, -47.08) * mm});
            skLineSegment(sketch, "E316.right", {"start": v(-105.08, -40.68) * mm, "end": v(-105.08, -47.08) * mm});
            skSolve(sketch);
        }
        {
            var Q0;
            Q0=makeQuery(id+"F0.imprint","IMPRINT",FACE,{"disambiguationData":[TD([[makeQuery(id+"F0.imprint","IMPRINT",EDGE,{"derivedFrom":sQuery(id+"F0.wireOp",EDGE,"E3")}),-1.0]])]});
            extrude(context, id + "F1", {"entities" : qUnion([Q0]), "depth" : 25 * mm, "offsetDistance" : 25 * mm});
        }
    });
